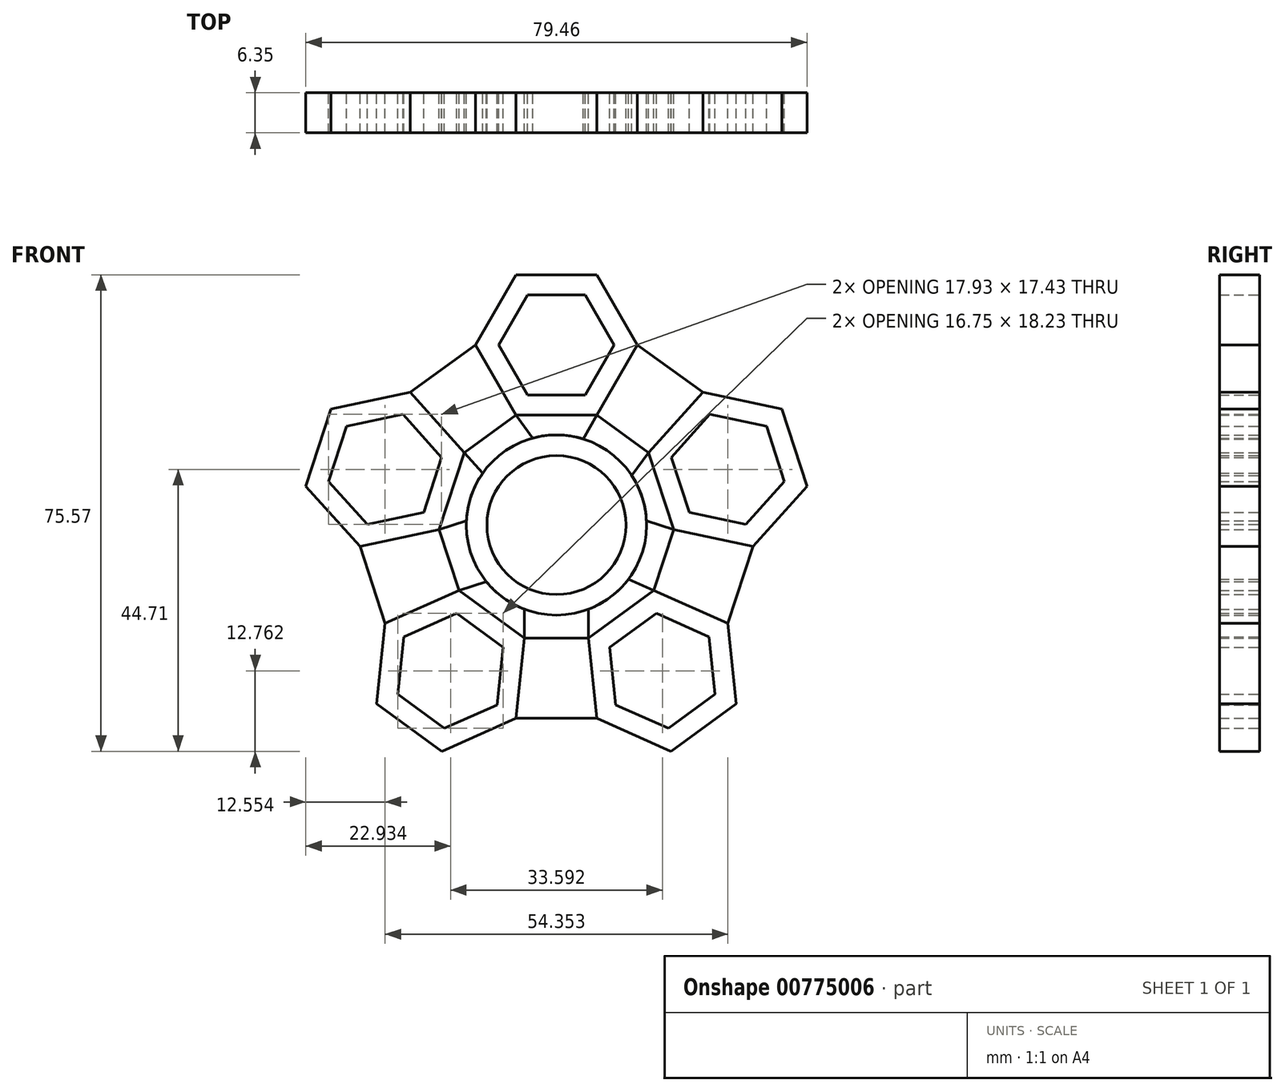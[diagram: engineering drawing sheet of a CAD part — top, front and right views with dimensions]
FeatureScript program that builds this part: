
annotation { "Feature Type Name" : "Feature", "Feature Type Description" : "" }
export const myFeature = defineFeature(function(context is Context, id is Id, definition is map)
    precondition{}
    {
        {
            var Q0;
            Q0=qCreatedBy(makeId("Front.planeOp"),FACE);
            var sketch = newSketch(context, id + "F0", { "sketchPlane" : qUnion([Q0])});
            skCircle(sketch, "E0", {"center": v(0, 0) * mm, "radius": 11.02 * mm});
            skCircle(sketch, "E1", {"center": v(0, 0) * mm, "radius": 14.29 * mm});
            skCircle(sketch, "E2.cCircle", {"center": v(0, 28.58) * mm, "radius": 11.11 * mm, "construction": true});
            skLineSegment(sketch, "E2.0", {"start": v(6.42, 17.46) * mm, "end": v(-6.42, 17.46) * mm});
            skLineSegment(sketch, "E2.1", {"start": v(-6.42, 17.46) * mm, "end": v(-12.83, 28.57) * mm});
            skLineSegment(sketch, "E2.2", {"start": v(-12.83, 28.57) * mm, "end": v(-6.42, 39.69) * mm});
            skLineSegment(sketch, "E2.3", {"start": v(-6.42, 39.69) * mm, "end": v(6.42, 39.69) * mm});
            skLineSegment(sketch, "E2.4", {"start": v(6.42, 39.69) * mm, "end": v(12.83, 28.58) * mm});
            skLineSegment(sketch, "E2.5", {"start": v(12.83, 28.58) * mm, "end": v(6.42, 17.46) * mm});
            skPoint(sketch, "E2.0.midPoint", {"position": v(0, 17.46) * mm});
            skCircle(sketch, "E3.cCircle", {"center": v(0, 28.58) * mm, "radius": 7.94 * mm, "construction": true});
            skLineSegment(sketch, "E3.0", {"start": v(4.58, 20.64) * mm, "end": v(-4.58, 20.64) * mm});
            skLineSegment(sketch, "E3.1", {"start": v(-4.58, 20.64) * mm, "end": v(-9.17, 28.57) * mm});
            skLineSegment(sketch, "E3.2", {"start": v(-9.17, 28.57) * mm, "end": v(-4.58, 36.51) * mm});
            skLineSegment(sketch, "E3.3", {"start": v(-4.58, 36.51) * mm, "end": v(4.58, 36.51) * mm});
            skLineSegment(sketch, "E3.4", {"start": v(4.58, 36.51) * mm, "end": v(9.17, 28.58) * mm});
            skLineSegment(sketch, "E3.5", {"start": v(9.17, 28.58) * mm, "end": v(4.58, 20.64) * mm});
            skPoint(sketch, "E3.0.midPoint", {"position": v(0, 20.64) * mm});
            skLineSegment(sketch, "E4.1.0", {"start": v(-14.63, 11.5) * mm, "end": v(-18.6, -0.7) * mm});
            skPoint(sketch, "E4.1.1", {"position": v(-19.63, 6.38) * mm});
            skLineSegment(sketch, "E4.1.2", {"start": v(-31.14, -3.37) * mm, "end": v(-39.73, 6.16) * mm});
            skLineSegment(sketch, "E4.1.3", {"start": v(-24.34, 17.55) * mm, "end": v(-18.21, 10.74) * mm});
            skLineSegment(sketch, "E4.1.4", {"start": v(-33.3, 15.64) * mm, "end": v(-24.34, 17.55) * mm});
            skLineSegment(sketch, "E4.1.5", {"start": v(-36.14, 6.92) * mm, "end": v(-33.3, 15.64) * mm});
            skLineSegment(sketch, "E4.1.6", {"start": v(-39.73, 6.16) * mm, "end": v(-35.76, 18.37) * mm});
            skLineSegment(sketch, "E4.1.7", {"start": v(-35.76, 18.37) * mm, "end": v(-23.21, 21.03) * mm});
            skLineSegment(sketch, "E4.1.8", {"start": v(-23.21, 21.03) * mm, "end": v(-14.63, 11.5) * mm});
            skCircle(sketch, "E4.1.9", {"center": v(-27.18, 8.83) * mm, "radius": 7.94 * mm, "construction": true});
            skLineSegment(sketch, "E4.1.10", {"start": v(-21.04, 2.02) * mm, "end": v(-30, 0.11) * mm});
            skLineSegment(sketch, "E4.1.11", {"start": v(-30, 0.11) * mm, "end": v(-36.14, 6.92) * mm});
            skPoint(sketch, "E4.1.12", {"position": v(-16.6, 5.4) * mm});
            skLineSegment(sketch, "E4.1.13", {"start": v(-18.21, 10.74) * mm, "end": v(-21.04, 2.02) * mm});
            skLineSegment(sketch, "E4.1.14", {"start": v(-18.6, -0.7) * mm, "end": v(-31.14, -3.37) * mm});
            skCircle(sketch, "E4.1.15", {"center": v(-27.18, 8.83) * mm, "radius": 11.11 * mm, "construction": true});
            skLineSegment(sketch, "E4.2.0", {"start": v(-15.45, -10.36) * mm, "end": v(-5.07, -17.9) * mm});
            skPoint(sketch, "E4.2.1", {"position": v(-12.13, -16.7) * mm});
            skLineSegment(sketch, "E4.2.2", {"start": v(-6.41, -30.66) * mm, "end": v(-18.14, -35.88) * mm});
            skLineSegment(sketch, "E4.2.3", {"start": v(-24.21, -17.73) * mm, "end": v(-15.84, -14) * mm});
            skLineSegment(sketch, "E4.2.4", {"start": v(-25.17, -26.85) * mm, "end": v(-24.21, -17.73) * mm});
            skLineSegment(sketch, "E4.2.5", {"start": v(-17.75, -32.23) * mm, "end": v(-25.17, -26.85) * mm});
            skLineSegment(sketch, "E4.2.6", {"start": v(-18.14, -35.88) * mm, "end": v(-28.52, -28.34) * mm});
            skLineSegment(sketch, "E4.2.7", {"start": v(-28.52, -28.34) * mm, "end": v(-27.18, -15.58) * mm});
            skLineSegment(sketch, "E4.2.8", {"start": v(-27.18, -15.58) * mm, "end": v(-15.45, -10.36) * mm});
            skCircle(sketch, "E4.2.9", {"center": v(-16.8, -23.12) * mm, "radius": 7.94 * mm, "construction": true});
            skLineSegment(sketch, "E4.2.10", {"start": v(-8.42, -19.39) * mm, "end": v(-9.38, -28.5) * mm});
            skLineSegment(sketch, "E4.2.11", {"start": v(-9.38, -28.5) * mm, "end": v(-17.75, -32.23) * mm});
            skPoint(sketch, "E4.2.12", {"position": v(-10.26, -14.13) * mm});
            skLineSegment(sketch, "E4.2.13", {"start": v(-15.84, -14) * mm, "end": v(-8.42, -19.39) * mm});
            skLineSegment(sketch, "E4.2.14", {"start": v(-5.07, -17.9) * mm, "end": v(-6.41, -30.66) * mm});
            skCircle(sketch, "E4.2.15", {"center": v(-16.8, -23.12) * mm, "radius": 11.11 * mm, "construction": true});
            skLineSegment(sketch, "E4.3.0", {"start": v(5.07, -17.9) * mm, "end": v(15.45, -10.36) * mm});
            skPoint(sketch, "E4.3.1", {"position": v(12.13, -16.7) * mm});
            skLineSegment(sketch, "E4.3.2", {"start": v(27.18, -15.58) * mm, "end": v(28.52, -28.34) * mm});
            skLineSegment(sketch, "E4.3.3", {"start": v(9.38, -28.5) * mm, "end": v(8.42, -19.39) * mm});
            skLineSegment(sketch, "E4.3.4", {"start": v(17.75, -32.23) * mm, "end": v(9.38, -28.5) * mm});
            skLineSegment(sketch, "E4.3.5", {"start": v(25.17, -26.85) * mm, "end": v(17.75, -32.23) * mm});
            skLineSegment(sketch, "E4.3.6", {"start": v(28.52, -28.34) * mm, "end": v(18.14, -35.88) * mm});
            skLineSegment(sketch, "E4.3.7", {"start": v(18.14, -35.88) * mm, "end": v(6.41, -30.66) * mm});
            skLineSegment(sketch, "E4.3.8", {"start": v(6.41, -30.66) * mm, "end": v(5.07, -17.9) * mm});
            skCircle(sketch, "E4.3.9", {"center": v(16.8, -23.12) * mm, "radius": 7.94 * mm, "construction": true});
            skLineSegment(sketch, "E4.3.10", {"start": v(15.84, -14) * mm, "end": v(24.21, -17.73) * mm});
            skLineSegment(sketch, "E4.3.11", {"start": v(24.21, -17.73) * mm, "end": v(25.17, -26.85) * mm});
            skPoint(sketch, "E4.3.12", {"position": v(10.26, -14.13) * mm});
            skLineSegment(sketch, "E4.3.13", {"start": v(8.42, -19.39) * mm, "end": v(15.84, -14) * mm});
            skLineSegment(sketch, "E4.3.14", {"start": v(15.45, -10.36) * mm, "end": v(27.18, -15.58) * mm});
            skCircle(sketch, "E4.3.15", {"center": v(16.8, -23.12) * mm, "radius": 11.11 * mm, "construction": true});
            skLineSegment(sketch, "E4.4.0", {"start": v(18.6, -0.7) * mm, "end": v(14.63, 11.5) * mm});
            skPoint(sketch, "E4.4.1", {"position": v(19.63, 6.38) * mm});
            skLineSegment(sketch, "E4.4.2", {"start": v(23.21, 21.03) * mm, "end": v(35.76, 18.37) * mm});
            skLineSegment(sketch, "E4.4.3", {"start": v(30, 0.11) * mm, "end": v(21.04, 2.02) * mm});
            skLineSegment(sketch, "E4.4.4", {"start": v(36.14, 6.92) * mm, "end": v(30, 0.11) * mm});
            skLineSegment(sketch, "E4.4.5", {"start": v(33.3, 15.64) * mm, "end": v(36.14, 6.92) * mm});
            skLineSegment(sketch, "E4.4.6", {"start": v(35.76, 18.37) * mm, "end": v(39.73, 6.16) * mm});
            skLineSegment(sketch, "E4.4.7", {"start": v(39.73, 6.16) * mm, "end": v(31.14, -3.37) * mm});
            skLineSegment(sketch, "E4.4.8", {"start": v(31.14, -3.37) * mm, "end": v(18.6, -0.7) * mm});
            skCircle(sketch, "E4.4.9", {"center": v(27.18, 8.83) * mm, "radius": 7.94 * mm, "construction": true});
            skLineSegment(sketch, "E4.4.10", {"start": v(18.21, 10.74) * mm, "end": v(24.34, 17.55) * mm});
            skLineSegment(sketch, "E4.4.11", {"start": v(24.34, 17.55) * mm, "end": v(33.3, 15.64) * mm});
            skPoint(sketch, "E4.4.12", {"position": v(16.6, 5.4) * mm});
            skLineSegment(sketch, "E4.4.13", {"start": v(21.04, 2.02) * mm, "end": v(18.21, 10.74) * mm});
            skLineSegment(sketch, "E4.4.14", {"start": v(14.63, 11.5) * mm, "end": v(23.21, 21.03) * mm});
            skCircle(sketch, "E4.4.15", {"center": v(27.18, 8.83) * mm, "radius": 11.11 * mm, "construction": true});
            skSolve(sketch);
        }
        {
            var Q0;
            Q0=qCreatedBy(makeId("Front.planeOp"),FACE);
            var sketch = newSketch(context, id + "F1", { "sketchPlane" : qUnion([Q0])});
            skLineSegment(sketch, "E5.0", {"start": v(24.34, 17.55) * mm, "end": v(33.3, 15.64) * mm});
            skLineSegment(sketch, "E5.1", {"start": v(36.14, 6.92) * mm, "end": v(30, 0.11) * mm});
            skLineSegment(sketch, "E5.2", {"start": v(-18.21, 10.74) * mm, "end": v(-21.04, 2.02) * mm});
            skLineSegment(sketch, "E5.3", {"start": v(23.21, 21.03) * mm, "end": v(35.76, 18.37) * mm});
            skCircle(sketch, "E5.4", {"center": v(-16.8, -23.12) * mm, "radius": 11.11 * mm});
            skLineSegment(sketch, "E5.5", {"start": v(-36.14, 6.92) * mm, "end": v(-33.3, 15.64) * mm});
            skLineSegment(sketch, "E5.6", {"start": v(-18.14, -35.88) * mm, "end": v(-28.52, -28.34) * mm});
            skLineSegment(sketch, "E5.7", {"start": v(6.41, -30.66) * mm, "end": v(5.07, -17.9) * mm});
            skLineSegment(sketch, "E5.8", {"start": v(18.21, 10.74) * mm, "end": v(24.34, 17.55) * mm});
            skLineSegment(sketch, "E5.9", {"start": v(-33.3, 15.64) * mm, "end": v(-24.34, 17.55) * mm});
            skLineSegment(sketch, "E5.10", {"start": v(-30, 0.11) * mm, "end": v(-36.14, 6.92) * mm});
            skLineSegment(sketch, "E5.11", {"start": v(-5.07, -17.9) * mm, "end": v(-6.41, -30.66) * mm});
            skLineSegment(sketch, "E5.12", {"start": v(18.6, -0.7) * mm, "end": v(14.63, 11.5) * mm});
            skLineSegment(sketch, "E5.13", {"start": v(27.18, -15.58) * mm, "end": v(28.52, -28.34) * mm});
            skCircle(sketch, "E5.14", {"center": v(16.8, -23.12) * mm, "radius": 7.94 * mm});
            skLineSegment(sketch, "E5.15", {"start": v(-28.52, -28.34) * mm, "end": v(-27.18, -15.58) * mm});
            skCircle(sketch, "E5.16", {"center": v(-27.18, 8.83) * mm, "radius": 11.11 * mm});
            skLineSegment(sketch, "E5.17", {"start": v(30, 0.11) * mm, "end": v(21.04, 2.02) * mm});
            skLineSegment(sketch, "E5.18", {"start": v(5.07, -17.9) * mm, "end": v(15.45, -10.36) * mm});
            skLineSegment(sketch, "E5.19", {"start": v(-18.6, -0.7) * mm, "end": v(-31.14, -3.37) * mm});
            skLineSegment(sketch, "E5.20", {"start": v(-39.73, 6.16) * mm, "end": v(-35.76, 18.37) * mm});
            skLineSegment(sketch, "E5.21", {"start": v(33.3, 15.64) * mm, "end": v(36.14, 6.92) * mm});
            skLineSegment(sketch, "E5.22", {"start": v(21.04, 2.02) * mm, "end": v(18.21, 10.74) * mm});
            skLineSegment(sketch, "E5.23", {"start": v(15.84, -14) * mm, "end": v(24.21, -17.73) * mm});
            skLineSegment(sketch, "E5.24", {"start": v(9.38, -28.5) * mm, "end": v(8.42, -19.39) * mm});
            skLineSegment(sketch, "E5.25", {"start": v(-15.45, -10.36) * mm, "end": v(-5.07, -17.9) * mm});
            skLineSegment(sketch, "E5.26", {"start": v(-27.18, -15.58) * mm, "end": v(-15.45, -10.36) * mm});
            skLineSegment(sketch, "E5.27", {"start": v(-35.76, 18.37) * mm, "end": v(-23.21, 21.03) * mm});
            skLineSegment(sketch, "E5.28", {"start": v(35.76, 18.37) * mm, "end": v(39.73, 6.16) * mm});
            skLineSegment(sketch, "E5.29", {"start": v(14.63, 11.5) * mm, "end": v(23.21, 21.03) * mm});
            skLineSegment(sketch, "E5.30", {"start": v(17.75, -32.23) * mm, "end": v(9.38, -28.5) * mm});
            skLineSegment(sketch, "E5.31", {"start": v(24.21, -17.73) * mm, "end": v(25.17, -26.85) * mm});
            skCircle(sketch, "E5.32", {"center": v(-16.8, -23.12) * mm, "radius": 7.94 * mm});
            skLineSegment(sketch, "E5.33", {"start": v(-6.41, -30.66) * mm, "end": v(-18.14, -35.88) * mm});
            skLineSegment(sketch, "E5.34", {"start": v(-4.58, 36.51) * mm, "end": v(4.58, 36.51) * mm});
            skLineSegment(sketch, "E5.35", {"start": v(4.58, 36.51) * mm, "end": v(9.17, 28.58) * mm});
            skLineSegment(sketch, "E5.36", {"start": v(9.17, 28.58) * mm, "end": v(4.58, 20.64) * mm});
            skCircle(sketch, "E5.37", {"center": v(0, 0) * mm, "radius": 11.02 * mm});
            skCircle(sketch, "E5.38", {"center": v(0, 0) * mm, "radius": 14.29 * mm});
            skCircle(sketch, "E5.39", {"center": v(0, 28.58) * mm, "radius": 11.11 * mm});
            skLineSegment(sketch, "E5.40", {"start": v(6.42, 17.46) * mm, "end": v(-6.42, 17.46) * mm});
            skLineSegment(sketch, "E5.41", {"start": v(-6.42, 17.46) * mm, "end": v(-12.83, 28.57) * mm});
            skLineSegment(sketch, "E5.42", {"start": v(-12.83, 28.57) * mm, "end": v(-6.42, 39.69) * mm});
            skLineSegment(sketch, "E5.43", {"start": v(-6.42, 39.69) * mm, "end": v(6.42, 39.69) * mm});
            skLineSegment(sketch, "E5.44", {"start": v(6.42, 39.69) * mm, "end": v(12.83, 28.58) * mm});
            skLineSegment(sketch, "E5.45", {"start": v(12.83, 28.58) * mm, "end": v(6.42, 17.46) * mm});
            skCircle(sketch, "E5.46", {"center": v(0, 28.58) * mm, "radius": 7.94 * mm});
            skLineSegment(sketch, "E5.47", {"start": v(4.58, 20.64) * mm, "end": v(-4.58, 20.64) * mm});
            skLineSegment(sketch, "E5.48", {"start": v(-4.58, 20.64) * mm, "end": v(-9.17, 28.57) * mm});
            skLineSegment(sketch, "E5.49", {"start": v(-9.17, 28.57) * mm, "end": v(-4.58, 36.51) * mm});
            skLineSegment(sketch, "E5.50", {"start": v(8.42, -19.39) * mm, "end": v(15.84, -14) * mm});
            skLineSegment(sketch, "E5.51", {"start": v(-8.42, -19.39) * mm, "end": v(-9.38, -28.5) * mm});
            skLineSegment(sketch, "E5.52", {"start": v(-23.21, 21.03) * mm, "end": v(-14.63, 11.5) * mm});
            skCircle(sketch, "E5.53", {"center": v(27.18, 8.83) * mm, "radius": 11.11 * mm});
            skLineSegment(sketch, "E5.54", {"start": v(-14.63, 11.5) * mm, "end": v(-18.6, -0.7) * mm});
            skLineSegment(sketch, "E5.55", {"start": v(39.73, 6.16) * mm, "end": v(31.14, -3.37) * mm});
            skLineSegment(sketch, "E5.56", {"start": v(25.17, -26.85) * mm, "end": v(17.75, -32.23) * mm});
            skLineSegment(sketch, "E5.57", {"start": v(-24.21, -17.73) * mm, "end": v(-15.84, -14) * mm});
            skLineSegment(sketch, "E5.58", {"start": v(15.45, -10.36) * mm, "end": v(27.18, -15.58) * mm});
            skLineSegment(sketch, "E5.59", {"start": v(-9.38, -28.5) * mm, "end": v(-17.75, -32.23) * mm});
            skCircle(sketch, "E5.60", {"center": v(-27.18, 8.83) * mm, "radius": 7.94 * mm});
            skLineSegment(sketch, "E5.61", {"start": v(-31.14, -3.37) * mm, "end": v(-39.73, 6.16) * mm});
            skLineSegment(sketch, "E5.62", {"start": v(31.14, -3.37) * mm, "end": v(18.6, -0.7) * mm});
            skLineSegment(sketch, "E5.63", {"start": v(28.52, -28.34) * mm, "end": v(18.14, -35.88) * mm});
            skLineSegment(sketch, "E5.64", {"start": v(-25.17, -26.85) * mm, "end": v(-24.21, -17.73) * mm});
            skCircle(sketch, "E5.65", {"center": v(16.8, -23.12) * mm, "radius": 11.11 * mm});
            skLineSegment(sketch, "E5.66", {"start": v(-15.84, -14) * mm, "end": v(-8.42, -19.39) * mm});
            skLineSegment(sketch, "E5.67", {"start": v(-21.04, 2.02) * mm, "end": v(-30, 0.11) * mm});
            skLineSegment(sketch, "E5.68", {"start": v(-24.34, 17.55) * mm, "end": v(-18.21, 10.74) * mm});
            skCircle(sketch, "E5.69", {"center": v(27.18, 8.83) * mm, "radius": 7.94 * mm});
            skLineSegment(sketch, "E5.70", {"start": v(18.14, -35.88) * mm, "end": v(6.41, -30.66) * mm});
            skLineSegment(sketch, "E5.71", {"start": v(-17.75, -32.23) * mm, "end": v(-25.17, -26.85) * mm});
            skLineSegment(sketch, "E6", {"start": v(-23.21, 21.03) * mm, "end": v(-12.83, 28.57) * mm});
            skLineSegment(sketch, "E7", {"start": v(12.83, 28.58) * mm, "end": v(23.21, 21.03) * mm});
            skLineSegment(sketch, "E8", {"start": v(31.14, -3.37) * mm, "end": v(27.18, -15.58) * mm});
            skLineSegment(sketch, "E9", {"start": v(6.41, -30.66) * mm, "end": v(-6.41, -30.66) * mm});
            skLineSegment(sketch, "E10", {"start": v(-27.18, -15.58) * mm, "end": v(-31.14, -3.37) * mm});
            skLineSegment(sketch, "E11", {"start": v(-18.6, -0.7) * mm, "end": v(-15.45, -10.36) * mm});
            skLineSegment(sketch, "E12", {"start": v(-5.07, -17.9) * mm, "end": v(5.07, -17.9) * mm});
            skLineSegment(sketch, "E13", {"start": v(15.45, -10.36) * mm, "end": v(18.6, -0.7) * mm});
            skLineSegment(sketch, "E14", {"start": v(14.63, 11.5) * mm, "end": v(6.42, 17.46) * mm});
            skLineSegment(sketch, "E15", {"start": v(-6.42, 17.46) * mm, "end": v(-14.63, 11.5) * mm});
            skLineSegment(sketch, "E16", {"start": v(-6.42, 17.46) * mm, "end": v(-3.75, 13.79) * mm});
            skLineSegment(sketch, "E17", {"start": v(6.42, 17.46) * mm, "end": v(4.22, 13.65) * mm});
            skLineSegment(sketch, "E18", {"start": v(-14.63, 11.5) * mm, "end": v(-11.68, 8.23) * mm});
            skLineSegment(sketch, "E19", {"start": v(14.63, 11.5) * mm, "end": v(11.96, 7.82) * mm});
            skLineSegment(sketch, "E20", {"start": v(-18.6, -0.7) * mm, "end": v(-14.27, 0.7) * mm});
            skLineSegment(sketch, "E21", {"start": v(-15.45, -10.36) * mm, "end": v(-11.13, -8.95) * mm});
            skLineSegment(sketch, "E22", {"start": v(5.07, -17.9) * mm, "end": v(5.07, -13.36) * mm});
            skLineSegment(sketch, "E23", {"start": v(15.45, -10.36) * mm, "end": v(11.43, -8.57) * mm});
            skLineSegment(sketch, "E24", {"start": v(18.6, -0.7) * mm, "end": v(14.27, 0.7) * mm});
            skLineSegment(sketch, "E25", {"start": v(-5.07, -17.9) * mm, "end": v(-5.07, -13.36) * mm});
            skSolve(sketch);
        }
        {
            var Q0;
            Q0=makeQuery(id+"F0.imprint","IMPRINT",FACE,{"disambiguationData":[TD([[makeQuery(id+"F0.imprint","IMPRINT",EDGE,{"derivedFrom":sQuery(id+"F0.wireOp",EDGE,"E2.0")}),-1.0]])]});
            var Q1;
            Q1=makeQuery(id+"F0.imprint","IMPRINT",FACE,{"disambiguationData":[TD([[makeQuery(id+"F0.imprint","IMPRINT",EDGE,{"derivedFrom":sQuery(id+"F0.wireOp",EDGE,"E4.1.0")}),-1.0]])]});
            var Q2;
            Q2=makeQuery(id+"F0.imprint","IMPRINT",FACE,{"disambiguationData":[TD([[makeQuery(id+"F0.imprint","IMPRINT",EDGE,{"derivedFrom":sQuery(id+"F0.wireOp",EDGE,"E4.2.0")}),-1.0]])]});
            var Q3;
            Q3=makeQuery(id+"F0.imprint","IMPRINT",FACE,{"disambiguationData":[TD([[makeQuery(id+"F0.imprint","IMPRINT",EDGE,{"derivedFrom":sQuery(id+"F0.wireOp",EDGE,"E4.3.0")}),-1.0]])]});
            var Q4;
            Q4=makeQuery(id+"F0.imprint","IMPRINT",FACE,{"disambiguationData":[TD([[makeQuery(id+"F0.imprint","IMPRINT",EDGE,{"derivedFrom":sQuery(id+"F0.wireOp",EDGE,"E4.4.0")}),-1.0]])]});
            var Q5;
            {var subQ0=sQuery(id+"F1.wireOp",EDGE,"E10");Q5=makeQuery(id+"F1.imprint","IMPRINT",FACE,{"disambiguationData":[TD([[makeQuery(id+"F1.imprint","IMPRINT",EDGE,{"derivedFrom":subQ0}),-1.0]])]});}
            var Q6;
            {var subQ0=sQuery(id+"F1.wireOp",EDGE,"E9");Q6=makeQuery(id+"F1.imprint","IMPRINT",FACE,{"disambiguationData":[TD([[makeQuery(id+"F1.imprint","IMPRINT",EDGE,{"derivedFrom":subQ0}),-1.0]])]});}
            var Q7;
            {var subQ3=sQuery(id+"F1.wireOp",EDGE,"E8");Q7=makeQuery(id+"F1.imprint","IMPRINT",FACE,{"disambiguationData":[TD([[makeQuery(id+"F1.imprint","IMPRINT",EDGE,{"derivedFrom":subQ3}),-1.0]])]});}
            var Q8;
            {var subQ3=sQuery(id+"F1.wireOp",EDGE,"E7");Q8=makeQuery(id+"F1.imprint","IMPRINT",FACE,{"disambiguationData":[TD([[makeQuery(id+"F1.imprint","IMPRINT",EDGE,{"derivedFrom":subQ3}),-1.0]])]});}
            var Q9;
            {var subQ3=sQuery(id+"F1.wireOp",EDGE,"E6");Q9=makeQuery(id+"F1.imprint","IMPRINT",FACE,{"disambiguationData":[TD([[makeQuery(id+"F1.imprint","IMPRINT",EDGE,{"derivedFrom":subQ3}),-1.0]])]});}
            var Q10;
            Q10=makeQuery(id+"F0.imprint","IMPRINT",FACE,{"disambiguationData":[TD([[makeQuery(id+"F0.imprint","IMPRINT",EDGE,{"derivedFrom":sQuery(id+"F0.wireOp",EDGE,"E0")}),-1.0]])]});
            var Q11;
            {var subQ0=sQuery(id+"F1.wireOp",EDGE,"E21");Q11=makeQuery(id+"F1.imprint","IMPRINT",FACE,{"disambiguationData":[TD([[makeQuery(id+"F1.imprint","IMPRINT",EDGE,{"derivedFrom":subQ0}),-1.0]])]});}
            var Q12;
            {var subQ0=sQuery(id+"F1.wireOp",EDGE,"E22");Q12=makeQuery(id+"F1.imprint","IMPRINT",FACE,{"disambiguationData":[TD([[makeQuery(id+"F1.imprint","IMPRINT",EDGE,{"derivedFrom":subQ0}),-1.0]])]});}
            var Q13;
            {var subQ0=sQuery(id+"F1.wireOp",EDGE,"E19");Q13=makeQuery(id+"F1.imprint","IMPRINT",FACE,{"disambiguationData":[TD([[makeQuery(id+"F1.imprint","IMPRINT",EDGE,{"derivedFrom":subQ0}),1.0]])]});}
            var Q14;
            {var subQ3=sQuery(id+"F1.wireOp",EDGE,"E18");Q14=makeQuery(id+"F1.imprint","IMPRINT",FACE,{"disambiguationData":[TD([[makeQuery(id+"F1.imprint","IMPRINT",EDGE,{"derivedFrom":subQ3}),-1.0]])]});}
            var Q15;
            {var subQ0=sQuery(id+"F1.wireOp",EDGE,"E16");Q15=makeQuery(id+"F1.imprint","IMPRINT",FACE,{"disambiguationData":[TD([[makeQuery(id+"F1.imprint","IMPRINT",EDGE,{"derivedFrom":subQ0}),1.0]])]});}
            extrude(context, id + "F2", {"entities" : qUnion([Q0, Q1, Q2, Q3, Q4, Q5, Q6, Q7, Q8, Q9, Q10, Q11, Q12, Q13, Q14, Q15]), "depth" : 6.35 * mm, "offsetDistance" : 25.4 * mm});
        }
    });
